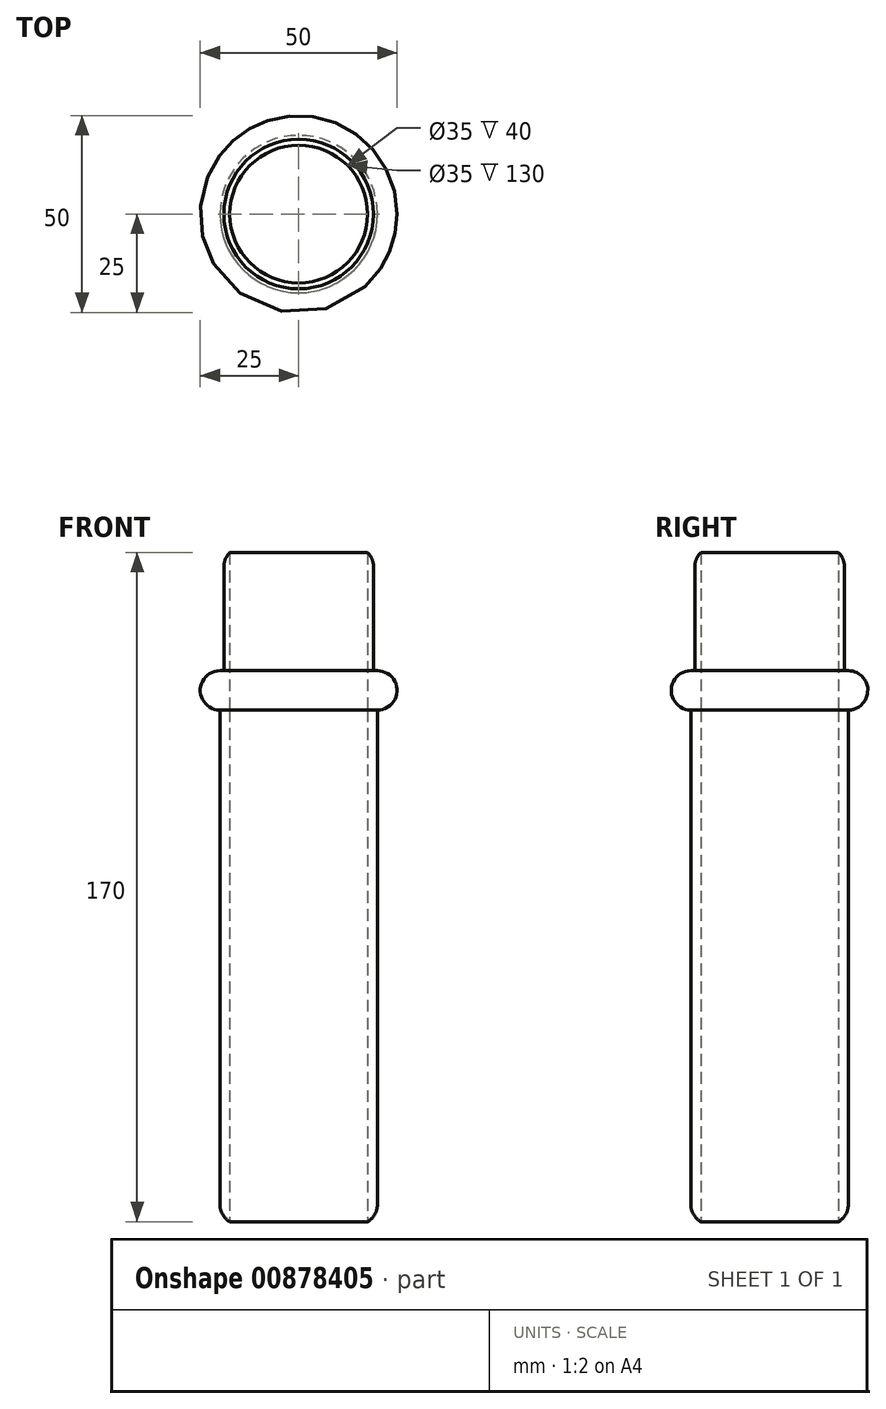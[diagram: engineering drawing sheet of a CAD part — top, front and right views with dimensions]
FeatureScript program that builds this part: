
annotation { "Feature Type Name" : "Feature", "Feature Type Description" : "" }
export const myFeature = defineFeature(function(context is Context, id is Id, definition is map)
    precondition{}
    {
        {
            var Q0;
            Q0=qCreatedBy(makeId("Top.planeOp"),FACE);
            var sketch = newSketch(context, id + "F0", { "sketchPlane" : qUnion([Q0])});
            skCircle(sketch, "E0", {"center": v(0, 0) * mm, "radius": 20 * mm});
            skCircle(sketch, "E1", {"center": v(0, 0) * mm, "radius": 17.5 * mm});
            skSolve(sketch);
        }
        {
            var Q0;
            Q0 = qSketchRegion(id + "F0", true);
            var Q1;
            Q1 = qSketchRegion(id + "F2", true);
            extrude(context, id + "F1", {"entities" : qUnion([Q0, Q1]), "depth" : 130 * mm, "offsetDistance" : 25 * mm});
        }
        {
            var Q0;
            Q0=makeQuery(id+"F1.opExtrude","CAP_FACE",FACE,{"disambiguationData":[OSD([sQuery(id+"F0.wireOp",EDGE,"E0"),sQuery(id+"F0.wireOp",EDGE,"E1")])],"isStart":false});
            var sketch = newSketch(context, id + "F2", { "sketchPlane" : qUnion([Q0])});
            skCircle(sketch, "E2", {"center": v(0, 0) * mm, "radius": 25 * mm});
            skSolve(sketch);
        }
        {
            var Q0;
            Q0=makeQuery(id+"F2.imprint","IMPRINT",FACE,{"disambiguationData":[TD([[makeQuery(id+"F2.imprint","IMPRINT",EDGE,{"derivedFrom":makeQuery(id+"F1.opExtrude","CAP_EDGE",EDGE,{"disambiguationData":[OSD([sQuery(id+"F0.wireOp",EDGE,"E0")])],"isStart":false})}),1.0]])]});
            var Q1;
            Q1=makeQuery(id+"F2.imprint","IMPRINT",FACE,{"disambiguationData":[TD([[makeQuery(id+"F2.imprint","IMPRINT",EDGE,{"derivedFrom":sQuery(id+"F2.wireOp",EDGE,"E2")}),1.0]])]});
            extrude(context, id + "F3", {"entities" : qUnion([Q0, Q1]), "depth" : 10 * mm, "offsetDistance" : 25 * mm});
        }
        {
            var Q0;
            Q0=makeQuery(id+"F3.opExtrude","CAP_FACE",FACE,{"disambiguationData":[OSD([sQuery(id+"F0.wireOp",EDGE,"E1"),sQuery(id+"F2.wireOp",EDGE,"E2")])],"isStart":false});
            var sketch = newSketch(context, id + "F4", { "sketchPlane" : qUnion([Q0])});
            skCircle(sketch, "E3", {"center": v(0, 0) * mm, "radius": 19 * mm});
            skSolve(sketch);
        }
        {
            var Q0;
            Q0=makeQuery(id+"F4.imprint","IMPRINT",FACE,{"disambiguationData":[TD([[makeQuery(id+"F4.imprint","IMPRINT",EDGE,{"derivedFrom":sQuery(id+"F4.wireOp",EDGE,"E3")}),1.0]])]});
            extrude(context, id + "F5", {"entities" : qUnion([Q0]), "operationType" : NewBodyOperationType.ADD, "depth" : 30 * mm, "offsetDistance" : 25 * mm});
        }
        {
            var Q0;
            Q0=makeQuery(id+"F3.opExtrude","CAP_EDGE",EDGE,{"disambiguationData":[OSD([sQuery(id+"F2.wireOp",EDGE,"E2")])],"isStart":false});
            var Q1;
            Q1=makeQuery(id+"F3.opExtrude","CAP_EDGE",EDGE,{"disambiguationData":[OSD([sQuery(id+"F2.wireOp",EDGE,"E2")])],"isStart":true});
            var Q2;
            Q2=makeQuery(id+"F1.opExtrude","CAP_EDGE",EDGE,{"disambiguationData":[OSD([sQuery(id+"F0.wireOp",EDGE,"E0")])],"isStart":true});
            fillet(context, id + "F6", {"entities" : qUnion([Q0, Q1, Q2]), "radius" : 5 * mm, "tangentPropagation" : true, "allowEdgeOverflow" : false});
        }
        {
            var Q0;
            Q0=makeQuery(id+"F5.opExtrude","CAP_EDGE",EDGE,{"disambiguationData":[OSD([sQuery(id+"F4.wireOp",EDGE,"E3")])],"isStart":false});
            fillet(context, id + "F7", {"entities" : qUnion([Q0]), "radius" : 5 * mm, "tangentPropagation" : true, "allowEdgeOverflow" : false});
        }
    });
